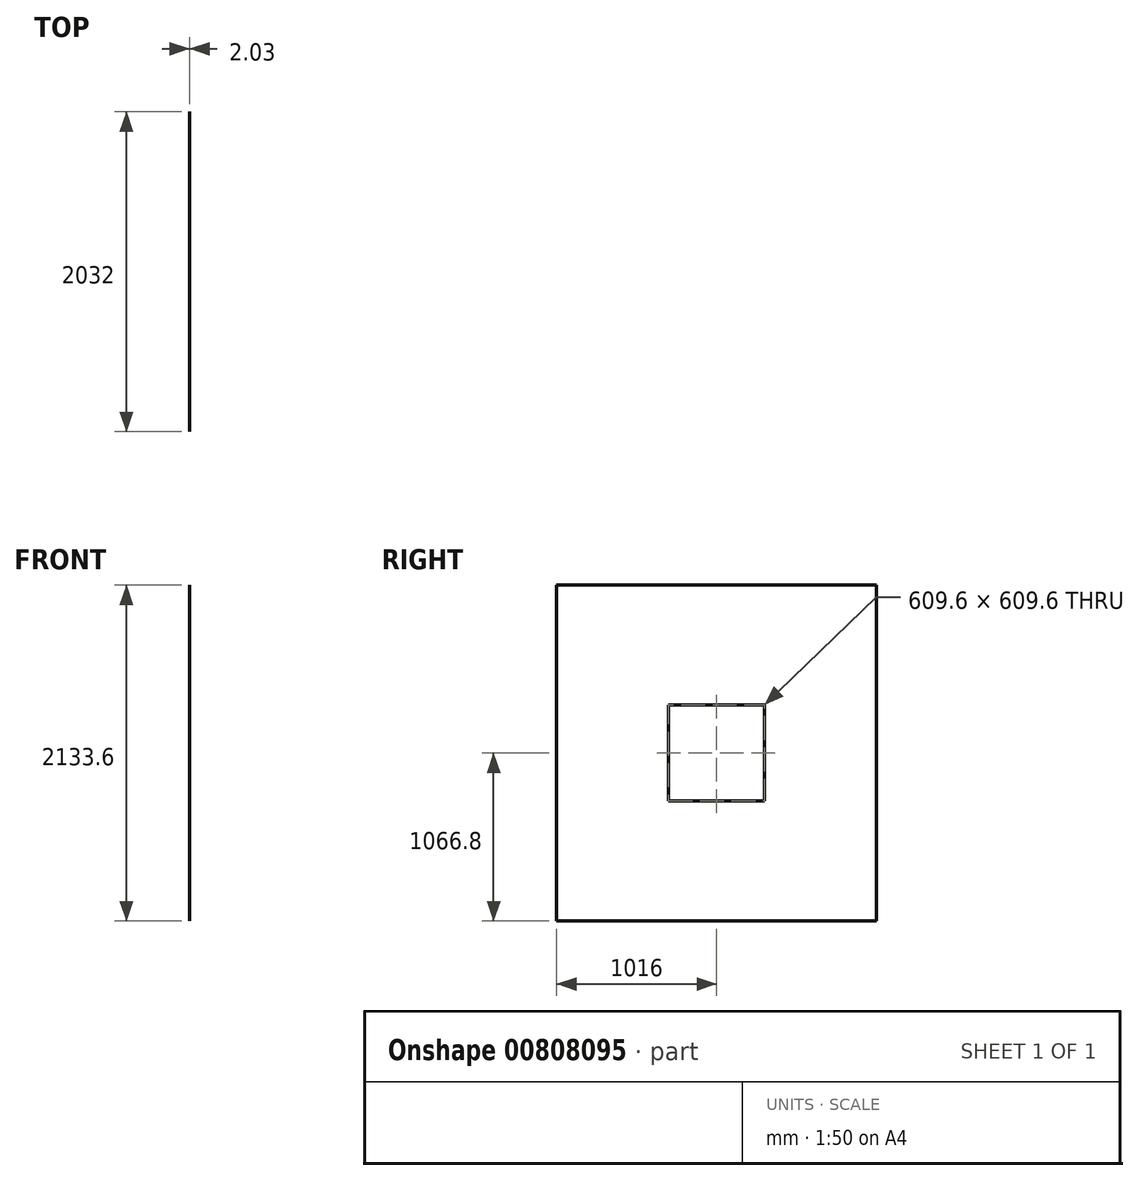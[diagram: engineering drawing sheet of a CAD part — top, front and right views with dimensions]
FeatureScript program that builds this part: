
annotation { "Feature Type Name" : "Feature", "Feature Type Description" : "" }
export const myFeature = defineFeature(function(context is Context, id is Id, definition is map)
    precondition{}
    {
        {
            var Q0;
            Q0=qCreatedBy(makeId("Front.planeOp"),FACE);
            var sketch = newSketch(context, id + "F0", { "sketchPlane" : qUnion([Q0])});
            skLineSegment(sketch, "E0", {"start": v(-3294.89, 1462.86) * mm, "end": v(-3292.86, 1462.86) * mm});
            skLineSegment(sketch, "E1", {"start": v(-3292.86, 1462.86) * mm, "end": v(-3292.86, -670.74) * mm});
            skLineSegment(sketch, "E2", {"start": v(-3292.86, -670.74) * mm, "end": v(-3294.89, -670.74) * mm});
            skLineSegment(sketch, "E3", {"start": v(-3294.89, 1462.86) * mm, "end": v(-3294.89, -670.74) * mm});
            skSolve(sketch);
        }
        {
            var Q0;
            Q0=qSketchRegion(id+"F0",true);
            extrude(context, id + "F1", {"entities" : qUnion([Q0]), "depth" : 2032 * mm, "offsetDistance" : 25.4 * mm});
        }
        {
            var Q0;
            Q0=makeQuery(id+"F1.opExtrude","SWEPT_FACE",FACE,{"disambiguationData":[OSD([sQuery(id+"F0.wireOp",EDGE,"E1")])]});
            var sketch = newSketch(context, id + "F2", { "sketchPlane" : qUnion([Q0])});
            skLineSegment(sketch, "E4.bottom", {"start": v(-1320.8, 700.86) * mm, "end": v(-711.2, 700.86) * mm});
            skLineSegment(sketch, "E4.top", {"start": v(-1320.8, 91.26) * mm, "end": v(-711.2, 91.26) * mm});
            skLineSegment(sketch, "E4.left", {"start": v(-1320.8, 700.86) * mm, "end": v(-1320.8, 91.26) * mm});
            skLineSegment(sketch, "E4.right", {"start": v(-711.2, 700.86) * mm, "end": v(-711.2, 91.26) * mm});
            skSolve(sketch);
        }
        {
            var Q0;
            Q0=makeQuery(id+"F2.imprint","IMPRINT",FACE,{"disambiguationData":[TD([[makeQuery(id+"F2.imprint","IMPRINT",EDGE,{"derivedFrom":sQuery(id+"F2.wireOp",EDGE,"E4.bottom")}),-1.0]])]});
            extrude(context, id + "F3", {"entities" : qUnion([Q0]), "operationType" : NewBodyOperationType.REMOVE, "oppositeDirection" : true, "depth" : 25.4 * mm, "offsetDistance" : 25.4 * mm});
        }
    });
